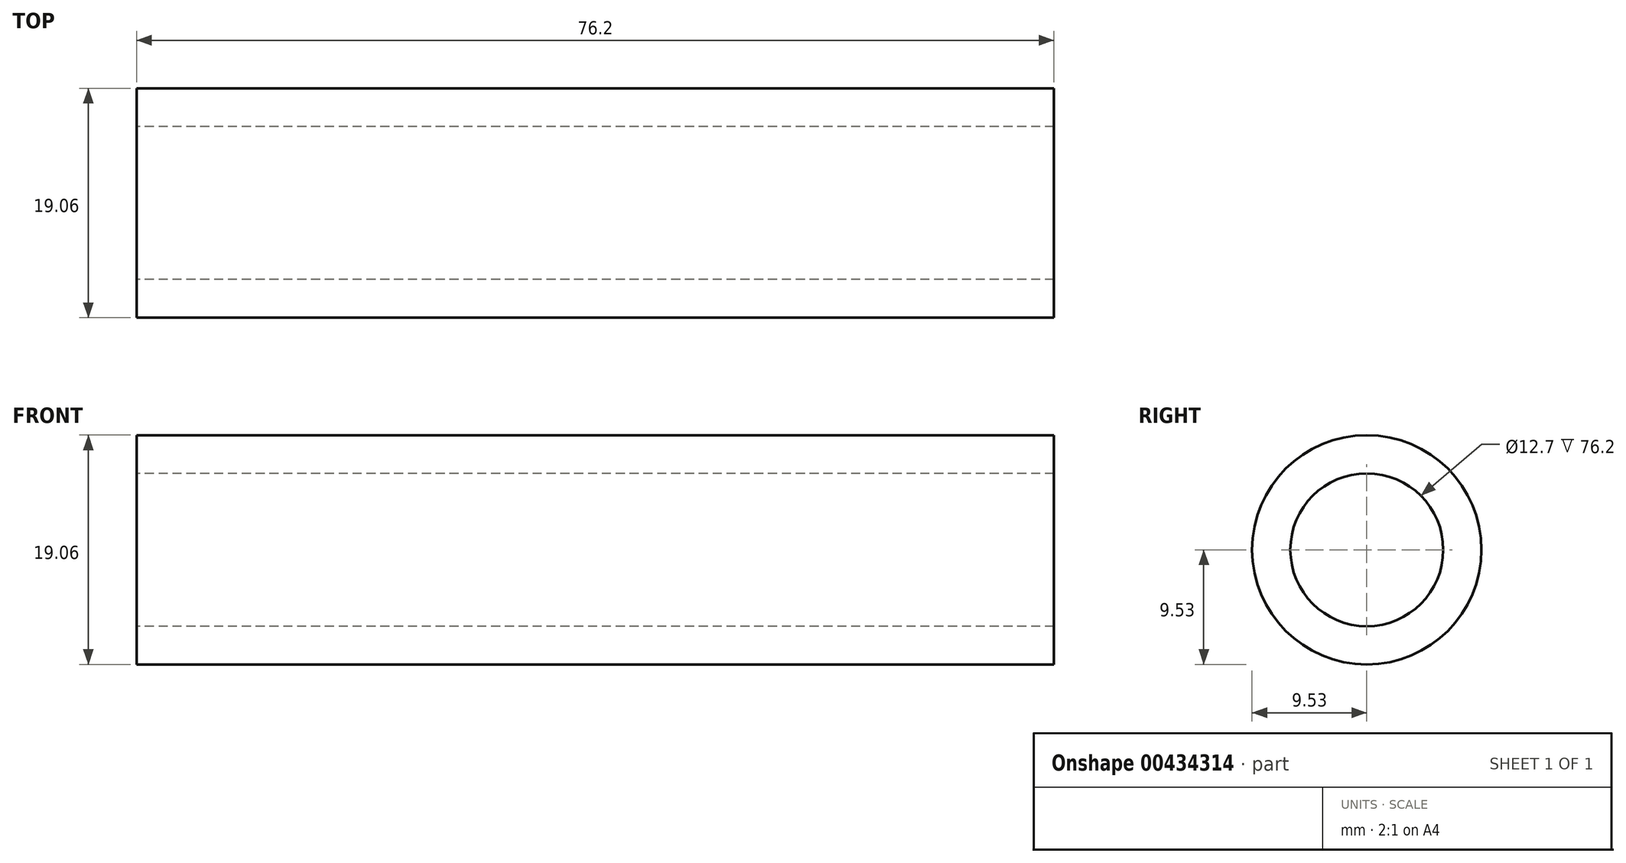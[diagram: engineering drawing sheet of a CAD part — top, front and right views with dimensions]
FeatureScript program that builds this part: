
annotation { "Feature Type Name" : "Feature", "Feature Type Description" : "" }
export const myFeature = defineFeature(function(context is Context, id is Id, definition is map)
    precondition{}
    {
        {
            var Q0;
            Q0=qCreatedBy(makeId("Right.planeOp"),FACE);
            var sketch = newSketch(context, id + "F0", { "sketchPlane" : qUnion([Q0])});
            skCircle(sketch, "E0", {"center": v(0, 0) * mm, "radius": 6.35 * mm});
            skCircle(sketch, "E1", {"center": v(0, 0) * mm, "radius": 9.53 * mm});
            skSolve(sketch);
        }
        {
            var Q0;
            Q0=makeQuery(id+"F0.imprint","IMPRINT",FACE,{"disambiguationData":[TD([[makeQuery(id+"F0.imprint","IMPRINT",EDGE,{"derivedFrom":sQuery(id+"F0.wireOp",EDGE,"E0")}),-1.0]])]});
            extrude(context, id + "F1", {"entities" : qUnion([Q0]), "endBound" : BoundingType.SYMMETRIC, "depth" : 76.2 * mm});
        }
    });
